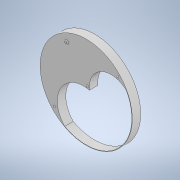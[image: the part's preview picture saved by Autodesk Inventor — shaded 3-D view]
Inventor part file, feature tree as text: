
AUTODESK INVENTOR PART (.ipt)
format: ipt  version: 2021 (Build 250183000, 183)  size: 138,240 bytes
history: native  units: mm
features: fillet x4, extrude x2, sketch x2
ambient origin geometry x8: Origin, YZ Plane, XZ Plane, XY Plane, X Axis, Y Axis, Z Axis, Center Point
bodies: Body1 (feature_tree)
feature tree (8):
  extrude  "Cadran"  Depth=54.0mm
  extrude  "Emplacements Vis"  Depth=54.5mm
  fillet  "Congé1"  Radius=5.0mm
  fillet  "Congé2"  Radius=1.369619mm
  fillet  "Congé3"  Radius=1.37mm
  fillet  "Congé4"  Radius=0.5mm
  sketch  "Esquisse1"
  sketch  "Esquisse4"
